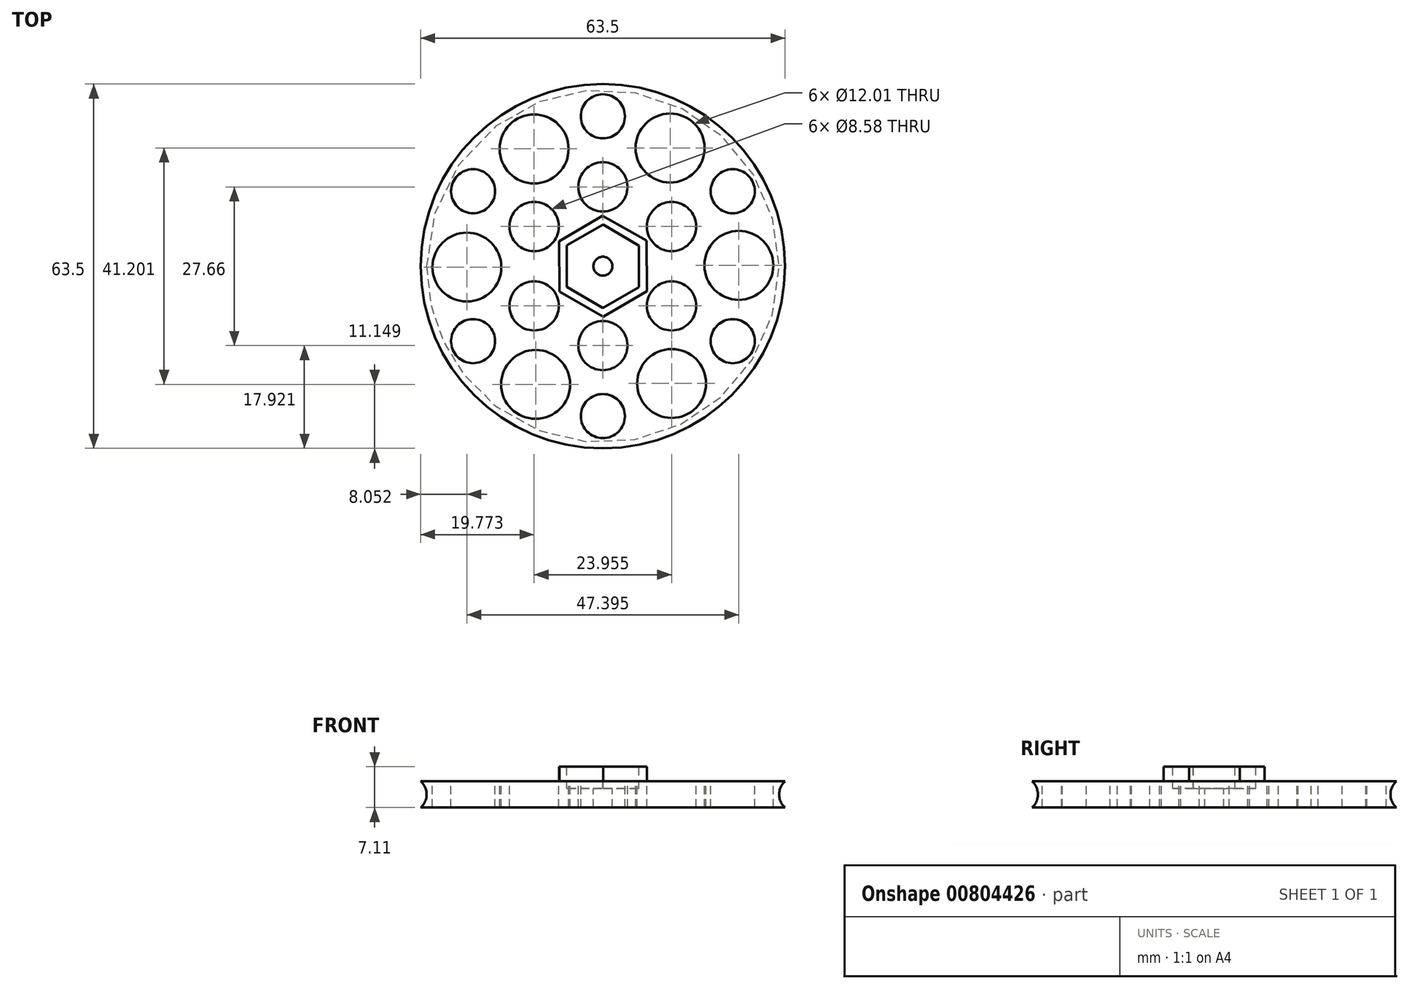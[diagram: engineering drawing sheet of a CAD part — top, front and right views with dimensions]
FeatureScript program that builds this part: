
annotation { "Feature Type Name" : "Feature", "Feature Type Description" : "" }
export const myFeature = defineFeature(function(context is Context, id is Id, definition is map)
    precondition{}
    {
        {
            var Q0;
            Q0=qCreatedBy(makeId("Front.planeOp"),FACE);
            var sketch = newSketch(context, id + "F0", { "sketchPlane" : qUnion([Q0])});
            skLineSegment(sketch, "E0", {"start": v(0, 0) * mm, "end": v(0, 4.57) * mm});
            skLineSegment(sketch, "E1", {"start": v(0, 4.57) * mm, "end": v(31.75, 4.57) * mm});
            skLineSegment(sketch, "E2", {"start": v(0, 0) * mm, "end": v(31.75, 0) * mm});
            skArc(sketch, "E3", {"start": v(31.75, 4.57) * mm, "mid": v(30.72, 2.29) * mm, "end": v(31.75, 0) * mm});
            skSolve(sketch);
        }
        {
            var Q0;
            Q0=makeQuery(id+"F0.imprint","IMPRINT",FACE,{"disambiguationData":[TD([[makeQuery(id+"F0.imprint","IMPRINT",EDGE,{"derivedFrom":sQuery(id+"F0.wireOp",EDGE,"E0")}),-1.0]])]});
            var Q1;
            Q1=sQuery(id+"F0.wireOp",EDGE,"E0");
            revolve(context, id + "F1", {"surfaceOperationType" : NewSurfaceOperationType.NEW, "entities" : qUnion([Q0]), "axis" : qUnion([Q1]), "revolveType" : RevolveType.FULL});
        }
        {
            var Q0;
            Q0=makeQuery(id+"F1.opRevolve","SWEPT_FACE",FACE,{"disambiguationData":[OSD([sQuery(id+"F0.wireOp",EDGE,"E1")])]});
            var sketch = newSketch(context, id + "F2", { "sketchPlane" : qUnion([Q0])});
            skCircle(sketch, "E4.cCircle", {"center": v(0, 0) * mm, "radius": 7.62 * mm, "construction": true});
            skLineSegment(sketch, "E4.0", {"start": v(-7.65, 4.35) * mm, "end": v(-0.06, 8.8) * mm});
            skLineSegment(sketch, "E4.1", {"start": v(-0.06, 8.8) * mm, "end": v(7.6, 4.45) * mm});
            skLineSegment(sketch, "E4.2", {"start": v(7.6, 4.45) * mm, "end": v(7.65, -4.35) * mm});
            skLineSegment(sketch, "E4.3", {"start": v(7.65, -4.35) * mm, "end": v(0.06, -8.8) * mm});
            skLineSegment(sketch, "E4.4", {"start": v(0.06, -8.8) * mm, "end": v(-7.6, -4.45) * mm});
            skLineSegment(sketch, "E4.5", {"start": v(-7.6, -4.45) * mm, "end": v(-7.65, 4.35) * mm});
            skPoint(sketch, "E4.0.midPoint", {"position": v(-3.85, 6.57) * mm});
            skSolve(sketch);
        }
        {
            var Q0;
            Q0=makeQuery(id+"F2.imprint","IMPRINT",FACE,{"disambiguationData":[TD([[makeQuery(id+"F2.imprint","IMPRINT",EDGE,{"derivedFrom":sQuery(id+"F2.wireOp",EDGE,"E4.0")}),-1.0]])]});
            extrude(context, id + "F3", {"entities" : qUnion([Q0]), "operationType" : NewBodyOperationType.ADD, "depth" : 2.54 * mm, "offsetDistance" : 25.4 * mm});
        }
        {
            var Q0;
            Q0=makeQuery(id+"F1.opRevolve","SWEPT_FACE",FACE,{"disambiguationData":[OSD([sQuery(id+"F0.wireOp",EDGE,"E1")])]});
            var sketch = newSketch(context, id + "F4", { "sketchPlane" : qUnion([Q0])});
            skCircle(sketch, "E5", {"center": v(0, 13.83) * mm, "radius": 4.3 * mm});
            skCircle(sketch, "E6", {"center": v(0, 26.12) * mm, "radius": 3.84 * mm});
            skCircle(sketch, "E7.1.0", {"center": v(-22.62, 13.06) * mm, "radius": 3.84 * mm});
            skCircle(sketch, "E7.1.1", {"center": v(-11.98, 6.91) * mm, "radius": 4.3 * mm});
            skCircle(sketch, "E7.2.0", {"center": v(-22.62, -13.06) * mm, "radius": 3.84 * mm});
            skCircle(sketch, "E7.2.1", {"center": v(-11.98, -6.92) * mm, "radius": 4.3 * mm});
            skCircle(sketch, "E7.3.0", {"center": v(0, -26.12) * mm, "radius": 3.84 * mm});
            skCircle(sketch, "E7.3.1", {"center": v(0, -13.83) * mm, "radius": 4.3 * mm});
            skCircle(sketch, "E7.4.0", {"center": v(22.62, -13.06) * mm, "radius": 3.84 * mm});
            skCircle(sketch, "E7.4.1", {"center": v(11.98, -6.91) * mm, "radius": 4.3 * mm});
            skCircle(sketch, "E7.5.0", {"center": v(22.62, 13.06) * mm, "radius": 3.84 * mm});
            skCircle(sketch, "E7.5.1", {"center": v(11.98, 6.92) * mm, "radius": 4.3 * mm});
            skPoint(sketch, "E7.center", {"position": v(0, 0) * mm});
            skCircle(sketch, "E8", {"center": v(0, 0) * mm, "radius": 26.12 * mm, "construction": true});
            skLineSegment(sketch, "E9", {"start": v(0, 0) * mm, "end": v(-13.21, 22.54) * mm, "construction": true});
            skCircle(sketch, "E10", {"center": v(-11.98, 20.44) * mm, "radius": 6 * mm});
            skCircle(sketch, "E11.1.0", {"center": v(-23.7, -0.16) * mm, "radius": 6 * mm});
            skCircle(sketch, "E11.2.0", {"center": v(-11.71, -20.6) * mm, "radius": 6 * mm});
            skCircle(sketch, "E11.3.0", {"center": v(11.98, -20.44) * mm, "radius": 6 * mm});
            skCircle(sketch, "E11.4.0", {"center": v(23.7, 0.16) * mm, "radius": 6 * mm});
            skCircle(sketch, "E11.5.0", {"center": v(11.71, 20.6) * mm, "radius": 6 * mm});
            skSolve(sketch);
        }
        {
            var Q0;
            Q0=makeQuery(id+"F4.imprint","IMPRINT",FACE,{"disambiguationData":[TD([[makeQuery(id+"F4.imprint","IMPRINT",EDGE,{"derivedFrom":sQuery(id+"F4.wireOp",EDGE,"E10")}),1.0]])]});
            var Q1;
            Q1=makeQuery(id+"F4.imprint","IMPRINT",FACE,{"disambiguationData":[TD([[makeQuery(id+"F4.imprint","IMPRINT",EDGE,{"derivedFrom":sQuery(id+"F4.wireOp",EDGE,"E5")}),1.0]])]});
            var Q2;
            Q2=makeQuery(id+"F4.imprint","IMPRINT",FACE,{"disambiguationData":[TD([[makeQuery(id+"F4.imprint","IMPRINT",EDGE,{"derivedFrom":sQuery(id+"F4.wireOp",EDGE,"E6")}),1.0]])]});
            var Q3;
            Q3=makeQuery(id+"F4.imprint","IMPRINT",FACE,{"disambiguationData":[TD([[makeQuery(id+"F4.imprint","IMPRINT",EDGE,{"derivedFrom":sQuery(id+"F4.wireOp",EDGE,"E11.5.0")}),1.0]])]});
            var Q4;
            Q4=makeQuery(id+"F4.imprint","IMPRINT",FACE,{"disambiguationData":[TD([[makeQuery(id+"F4.imprint","IMPRINT",EDGE,{"derivedFrom":sQuery(id+"F4.wireOp",EDGE,"E7.5.1")}),1.0]])]});
            var Q5;
            Q5=makeQuery(id+"F4.imprint","IMPRINT",FACE,{"disambiguationData":[TD([[makeQuery(id+"F4.imprint","IMPRINT",EDGE,{"derivedFrom":sQuery(id+"F4.wireOp",EDGE,"E11.4.0")}),1.0]])]});
            var Q6;
            Q6=makeQuery(id+"F4.imprint","IMPRINT",FACE,{"disambiguationData":[TD([[makeQuery(id+"F4.imprint","IMPRINT",EDGE,{"derivedFrom":sQuery(id+"F4.wireOp",EDGE,"E7.4.0")}),1.0]])]});
            var Q7;
            Q7=makeQuery(id+"F4.imprint","IMPRINT",FACE,{"disambiguationData":[TD([[makeQuery(id+"F4.imprint","IMPRINT",EDGE,{"derivedFrom":sQuery(id+"F4.wireOp",EDGE,"E7.4.1")}),1.0]])]});
            var Q8;
            Q8=makeQuery(id+"F4.imprint","IMPRINT",FACE,{"disambiguationData":[TD([[makeQuery(id+"F4.imprint","IMPRINT",EDGE,{"derivedFrom":sQuery(id+"F4.wireOp",EDGE,"E11.3.0")}),1.0]])]});
            var Q9;
            Q9=makeQuery(id+"F4.imprint","IMPRINT",FACE,{"disambiguationData":[TD([[makeQuery(id+"F4.imprint","IMPRINT",EDGE,{"derivedFrom":sQuery(id+"F4.wireOp",EDGE,"E7.3.0")}),1.0]])]});
            var Q10;
            Q10=makeQuery(id+"F4.imprint","IMPRINT",FACE,{"disambiguationData":[TD([[makeQuery(id+"F4.imprint","IMPRINT",EDGE,{"derivedFrom":sQuery(id+"F4.wireOp",EDGE,"E7.3.1")}),1.0]])]});
            var Q11;
            Q11=makeQuery(id+"F4.imprint","IMPRINT",FACE,{"disambiguationData":[TD([[makeQuery(id+"F4.imprint","IMPRINT",EDGE,{"derivedFrom":sQuery(id+"F4.wireOp",EDGE,"E11.2.0")}),1.0]])]});
            var Q12;
            Q12=makeQuery(id+"F4.imprint","IMPRINT",FACE,{"disambiguationData":[TD([[makeQuery(id+"F4.imprint","IMPRINT",EDGE,{"derivedFrom":sQuery(id+"F4.wireOp",EDGE,"E7.2.1")}),1.0]])]});
            var Q13;
            Q13=makeQuery(id+"F4.imprint","IMPRINT",FACE,{"disambiguationData":[TD([[makeQuery(id+"F4.imprint","IMPRINT",EDGE,{"derivedFrom":sQuery(id+"F4.wireOp",EDGE,"E11.1.0")}),1.0]])]});
            var Q14;
            Q14=makeQuery(id+"F4.imprint","IMPRINT",FACE,{"disambiguationData":[TD([[makeQuery(id+"F4.imprint","IMPRINT",EDGE,{"derivedFrom":sQuery(id+"F4.wireOp",EDGE,"E7.1.0")}),1.0]])]});
            var Q15;
            Q15=makeQuery(id+"F4.imprint","IMPRINT",FACE,{"disambiguationData":[TD([[makeQuery(id+"F4.imprint","IMPRINT",EDGE,{"derivedFrom":sQuery(id+"F4.wireOp",EDGE,"E7.1.1")}),1.0]])]});
            var Q16;
            Q16=makeQuery(id+"F4.imprint","IMPRINT",FACE,{"disambiguationData":[TD([[makeQuery(id+"F4.imprint","IMPRINT",EDGE,{"derivedFrom":sQuery(id+"F4.wireOp",EDGE,"E7.2.0")}),1.0]])]});
            var Q17;
            Q17=makeQuery(id+"F4.imprint","IMPRINT",FACE,{"disambiguationData":[TD([[makeQuery(id+"F4.imprint","IMPRINT",EDGE,{"derivedFrom":sQuery(id+"F4.wireOp",EDGE,"E7.5.0")}),1.0]])]});
            extrude(context, id + "F5", {"entities" : qUnion([Q0, Q1, Q2, Q3, Q4, Q5, Q6, Q7, Q8, Q9, Q10, Q11, Q12, Q13, Q14, Q15, Q16, Q17]), "operationType" : NewBodyOperationType.REMOVE, "oppositeDirection" : true, "depth" : 25.4 * mm, "offsetDistance" : 25.4 * mm});
        }
        {
            var Q0;
            Q0=makeQuery(id+"F3.opExtrude","CAP_FACE",FACE,{"disambiguationData":[OSD([sQuery(id+"F2.wireOp",EDGE,"E4.0"),sQuery(id+"F2.wireOp",EDGE,"E4.1"),sQuery(id+"F2.wireOp",EDGE,"E4.2"),sQuery(id+"F2.wireOp",EDGE,"E4.3"),sQuery(id+"F2.wireOp",EDGE,"E4.4"),sQuery(id+"F2.wireOp",EDGE,"E4.5")])],"isStart":false});
            var sketch = newSketch(context, id + "F6", { "sketchPlane" : qUnion([Q0])});
            skCircle(sketch, "E12.cCircle", {"center": v(0, 0) * mm, "radius": 6.29 * mm, "construction": true});
            skLineSegment(sketch, "E12.0", {"start": v(0.03, 7.26) * mm, "end": v(6.3, 3.6) * mm});
            skLineSegment(sketch, "E12.1", {"start": v(6.3, 3.6) * mm, "end": v(6.27, -3.65) * mm});
            skLineSegment(sketch, "E12.2", {"start": v(6.27, -3.65) * mm, "end": v(-0.03, -7.26) * mm});
            skLineSegment(sketch, "E12.3", {"start": v(-0.03, -7.26) * mm, "end": v(-6.3, -3.6) * mm});
            skLineSegment(sketch, "E12.4", {"start": v(-6.3, -3.6) * mm, "end": v(-6.27, 3.65) * mm});
            skLineSegment(sketch, "E12.5", {"start": v(-6.27, 3.65) * mm, "end": v(0.03, 7.26) * mm});
            skPoint(sketch, "E12.0.midPoint", {"position": v(3.16, 5.43) * mm});
            skSolve(sketch);
        }
        {
            var Q0;
            Q0 = qSketchRegion(id + "F6", true);
            extrude(context, id + "F7", {"entities" : qUnion([Q0]), "operationType" : NewBodyOperationType.REMOVE, "oppositeDirection" : true, "depth" : 3.8 * mm, "offsetDistance" : 25.4 * mm});
        }
        {
            var Q0;
            Q0=makeQuery(id+"F7.boolean.opBoolean","COPY",FACE,{"derivedFrom":makeQuery(id+"F7.opExtrude","CAP_FACE",FACE,{"disambiguationData":[OSD([sQuery(id+"F6.wireOp",EDGE,"E12.0"),sQuery(id+"F6.wireOp",EDGE,"E12.1"),sQuery(id+"F6.wireOp",EDGE,"E12.2"),sQuery(id+"F6.wireOp",EDGE,"E12.3"),sQuery(id+"F6.wireOp",EDGE,"E12.4"),sQuery(id+"F6.wireOp",EDGE,"E12.5")])],"isStart":false})});
            var sketch = newSketch(context, id + "F8", { "sketchPlane" : qUnion([Q0])});
            skCircle(sketch, "E13", {"center": v(0, 0) * mm, "radius": 1.65 * mm});
            skSolve(sketch);
        }
        {
            var Q0;
            Q0=makeQuery(id+"F8.imprint","IMPRINT",FACE,{"disambiguationData":[TD([[makeQuery(id+"F8.imprint","IMPRINT",EDGE,{"derivedFrom":sQuery(id+"F8.wireOp",EDGE,"E13")}),1.0]])]});
            var Q1;
            Q1=sQuery(id+"F8.wireOp",EDGE,"E13");
            extrude(context, id + "F9", {"entities" : qUnion([Q0]), "operationType" : NewBodyOperationType.REMOVE, "surfaceEntities" : qUnion([Q1]), "oppositeDirection" : true, "depth" : 25.4 * mm, "offsetDistance" : 25.4 * mm});
        }
    });
